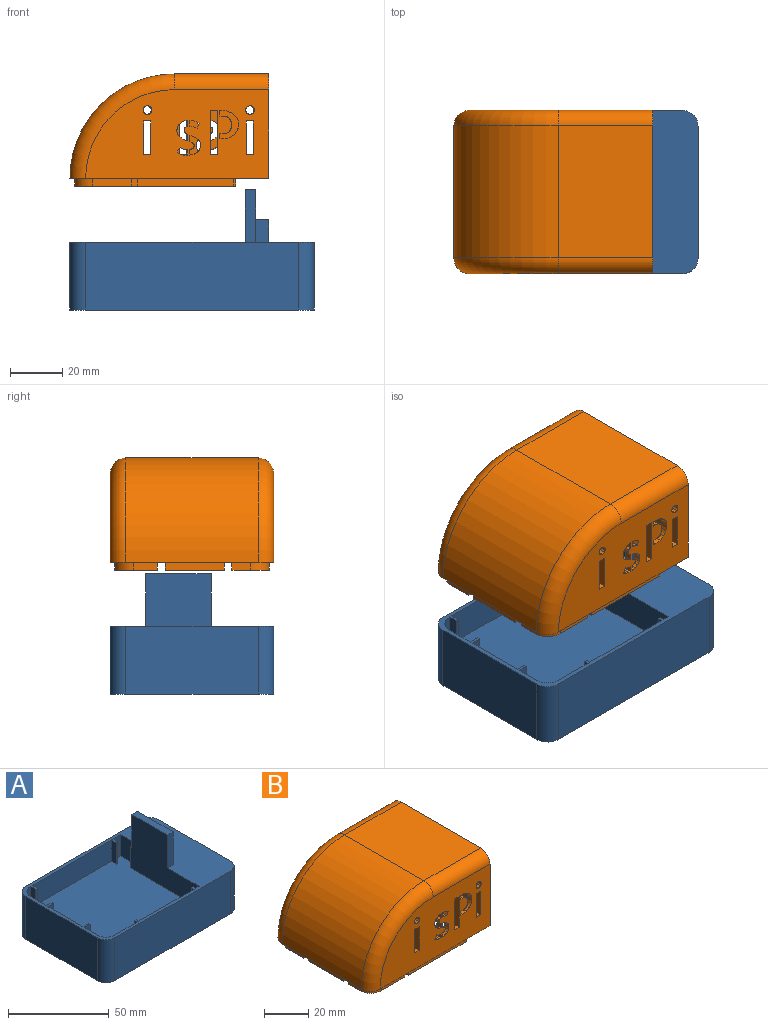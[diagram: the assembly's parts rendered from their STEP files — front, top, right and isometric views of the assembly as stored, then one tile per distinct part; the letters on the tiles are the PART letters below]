
ASSEMBLY  parts=2 mates=1
PART A: 51 faces, bbox 93.5x62.6x46 mm
  f0: plane 93.5x62.6mm, normal (0,0,1), area 1803.2mm2, adj f1,f2,f3,f4,f5,f6,f7,f8
  f1: plane 81.5x26mm, normal (0,-1,0), area 2119mm2, adj f0,f2,f40,f41
  f2: cylinder r=6mm len=26mm, axis (0,0,-1), area 245mm2, adj f0,f1,f3,f41
  f3: plane 50.6x26mm, normal (1,0,0), area 1315.6mm2, adj f0,f2,f4,f41
  f4: cylinder r=6mm len=26mm, axis (0,0,-1), area 245mm2, adj f0,f3,f5,f41
  f5: plane 81.5x26mm, normal (0,1,0), area 2119mm2, adj f0,f4,f6,f41
  f6: cylinder r=6mm len=26mm, axis (0,0,-1), area 245mm2, adj f0,f5,f7,f41
  f7: plane 50.6x26mm, normal (-1,0,0), area 1315.6mm2, adj f0,f6,f40,f41
  f8: plane 24.6x13mm, normal (1,0,0), area 319.8mm2, adj f0,f9,f39,f50
  f9: plane 13x4mm, normal (0,-1,0), area 52mm2, adj f0,f8,f10,f50
  f10: plane 13x1mm, normal (1,0,0), area 13mm2, adj f0,f9,f11,f50
  f11: plane 13x4mm, normal (0,1,0), area 52mm2, adj f0,f10,f12,f50
  f12: plane 13x11.25mm, normal (1,0,0), area 146.2mm2, adj f0,f11,f13,f50
  f13: cylinder r=6mm len=13mm, axis (0,0,-1), area 122.5mm2, adj f0,f12,f14,f50
  f14: plane 13x0.25mm, normal (0,-1,0), area 3.3mm2, adj f0,f13,f15,f50
  f15: plane 13x3.5mm, normal (-1,0,0), area 45.5mm2, adj f0,f14,f16,f50
  f16: plane 13x1mm, normal (0,-1,0), area 13mm2, adj f0,f15,f17,f50
  f17: plane 13x3.5mm, normal (1,0,0), area 45.5mm2, adj f0,f16,f18,f50
  f18: plane 55.6x13mm, normal (0,-1,0), area 722.8mm2, adj f0,f17,f19,f50
  f19: plane 13x3.5mm, normal (-1,0,0), area 45.5mm2, adj f0,f18,f20,f50
  f20: plane 13x1mm, normal (0,-1,0), area 13mm2, adj f0,f19,f21,f50
  f21: plane 13x3.5mm, normal (1,0,0), area 45.5mm2, adj f0,f20,f22,f50
  f22: plane 13x5.6mm, normal (0,-1,0), area 72.8mm2, adj f0,f21,f23,f50
  f23: plane 13x10.6mm, normal (-1,0,0), area 137.8mm2, adj f0,f22,f24,f50
  f24: plane 13x4mm, normal (0,1,0), area 52mm2, adj f0,f23,f25,f50
  f25: plane 48.5x33mm, normal (-1,0,0), area 1130.5mm2, adj f0,f24,f26,f43,f44,f45,f50
  f26: plane 13x2.5mm, normal (0,1,0), area 32.5mm2, adj f0,f25,f27,f50
  f27: plane 13x1.8mm, normal (1,0,0), area 23.4mm2, adj f0,f26,f28,f50
  f28: plane 13x1mm, normal (0,1,0), area 13mm2, adj f0,f27,f29,f50
  f29: plane 13x1.8mm, normal (-1,0,0), area 23.4mm2, adj f0,f28,f30,f50
  f30: plane 39x13mm, normal (0,1,0), area 507mm2, adj f0,f29,f31,f50
  f31: plane 13x1.8mm, normal (1,0,0), area 23.4mm2, adj f0,f30,f32,f50
  f32: plane 13x0.95mm, normal (0,1,0), area 12.3mm2, adj f0,f31,f33,f50
  f33: plane 13x1.8mm, normal (-1,0,0), area 23.4mm2, adj f0,f32,f34,f50
  f34: plane 16x13mm, normal (0,1,0), area 208mm2, adj f0,f33,f35,f50
  f35: cylinder r=6mm len=13mm, axis (0,0,-1), area 122.5mm2, adj f0,f34,f36,f50
  f36: plane 13x9.25mm, normal (1,0,0), area 120.3mm2, adj f0,f35,f37,f50
  f37: plane 13x4mm, normal (0,-1,0), area 52mm2, adj f0,f36,f38,f50
  f38: plane 13x1mm, normal (1,0,0), area 13mm2, adj f0,f37,f39,f50
  f39: plane 13x4mm, normal (0,1,0), area 52mm2, adj f0,f8,f38,f50
  f40: cylinder r=6mm len=26mm, axis (0,0,-1), area 245mm2, adj f0,f1,f7,f41
  f41: plane 93.5x62.6mm, normal (0,0,-1), area 5822.2mm2, adj f1,f2,f3,f4,f5,f6,f7,f40
  f42: plane 25x20mm, normal (1,0,0), area 427.7mm2, adj f0,f43,f44,f45,f46,f47,f49
  f43: plane 20x4mm, normal (0,1,0), area 80mm2, adj f0,f25,f42,f45
  f44: plane 20x4mm, normal (0,-1,0), area 80mm2, adj f0,f25,f42,f45
  f45: plane 25x4mm, normal (0,0,1), area 100mm2, adj f25,f42,f43,f44
  f46: plane 8.5x5mm, normal (0,1,0), area 42.5mm2, adj f0,f42,f48,f49
  f47: plane 8.5x5mm, normal (0,-1,0), area 42.5mm2, adj f0,f42,f48,f49
  f48: plane 8.5x8.5mm, normal (1,0,0), area 72.3mm2, adj f0,f46,f47,f49
  f49: plane 8.5x5mm, normal (0,0,1), area 42.5mm2, adj f42,f46,f47,f48
  f50: plane 69.45x59.1mm, normal (0,0,1), area 3876.5mm2, adj f8,f9,f10,f11,f12,f13,f14,f15
PART B: 242 faces, bbox 79.5x62.6x46.3 mm
  f0: plane 65.45x34.25mm, normal (0,1,0), area 1760mm2, adj f5,f6,f7,f11,f29,f30,f35,f36
  f1: plane 70.2x34mm, normal (0,-1,0), area 1907.2mm2, adj f4,f6,f17,f20,f149,f150,f151,f152
  f2: plane 66.2x35mm, normal (0,-1,0), area 1828mm2, adj f5,f6,f10,f14,f24,f25,f27,f56
  f3: plane 70.2x34mm, normal (0,1,0), area 1907.2mm2, adj f4,f6,f15,f18,f56,f57,f58,f59
  f4: plane 62.6x40mm, normal (1,0,0), area 1909.3mm2, adj f1,f3,f6,f18,f19,f20,f21,f22
  f5: plane 57.1x37.25mm, normal (-1,0,0), area 1532.3mm2, adj f0,f2,f6,f7,f8,f9,f10,f21
  f6: plane 76.2x62.6mm, normal (0,0,-1), area 510mm2, adj f0,f1,f2,f3,f4,f5,f12,f13
  f7: cylinder r=6mm len=34.2mm, axis (-1,0,0), area 322.3mm2, adj f0,f5,f8,f11
  f8: plane 45.1x34.2mm, normal (0,0,-1), area 1542.4mm2, adj f5,f7,f9,f12
  f9: cylinder r=6mm len=34.2mm, axis (-1,0,0), area 296.6mm2, adj f5,f8,f10,f13
  f10: plane 34.2x0.05mm, normal (0,0,-1), area 1.6mm2, adj f2,f5,f9,f14
  f11: torus R=31.25mm, axis (0,-1,0), area 519.2mm2, adj f0,f7,f12,f30
  f12: cylinder r=37.25mm len=45.1mm, axis (0,-1,0), area 2638.9mm2, adj f6,f8,f11,f13,f31,f45,f47
  f13: torus R=31.25mm, axis (0,-1,0), area 481.8mm2, adj f6,f9,f12,f14,f40
  f14: cylinder r=32mm len=32mm, axis (0,-1,0), area 2.4mm2, adj f2,f6,f10,f13
  f15: torus R=34mm, axis (0,-1,0), area 559.9mm2, adj f3,f6,f16,f18
  f16: cylinder r=40mm len=50.6mm, axis (0,-1,0), area 3179.3mm2, adj f6,f15,f17,f19
  f17: torus R=34mm, axis (0,-1,0), area 559.9mm2, adj f1,f6,f16,f20
  f18: cylinder r=6mm len=36.2mm, axis (-1,0,0), area 341.2mm2, adj f3,f4,f15,f19
  f19: plane 50.6x36.2mm, normal (0,0,1), area 1831.7mm2, adj f4,f16,f18,f20
  f20: cylinder r=6mm len=36.2mm, axis (-1,0,0), area 341.2mm2, adj f1,f4,f17,f19
  f21: plane 8.5x2mm, normal (0,1,0), area 17mm2, adj f4,f5,f6,f23
  f22: plane 8.5x2mm, normal (0,-1,0), area 17mm2, adj f4,f5,f6,f23
  f23: plane 8.5x2mm, normal (0,0,-1), area 17mm2, adj f4,f5,f21,f22
  f24: plane 3x1mm, normal (-1,0,0), area 3mm2, adj f2,f6,f26,f27
  f25: plane 3x1mm, normal (1,0,0), area 3mm2, adj f2,f6,f26,f27
  f26: plane 53.6x3mm, normal (0,1,0), area 160.8mm2, adj f6,f24,f25,f27
  f27: plane 53.6x1mm, normal (0,0,-1), area 53.6mm2, adj f2,f24,f25,f26
  f28: plane 14.95x3mm, normal (0,-1,0), area 44.8mm2, adj f6,f29,f34,f35
  f29: plane 3x1mm, normal (1,0,0), area 3mm2, adj f0,f6,f28,f35
  f30: cylinder r=6mm len=6mm, axis (0,0,1), area 28.3mm2, adj f0,f11,f31,f35
  f31: plane 7.25x3mm, normal (1,0,0), area 21.8mm2, adj f12,f30,f32,f35
  f32: plane 3x1mm, normal (0,1,0), area 3mm2, adj f6,f31,f33,f35
  f33: plane 7.25x3mm, normal (-1,0,0), area 21.8mm2, adj f6,f32,f34,f35
  f34: cylinder r=7mm len=7mm, axis (0,0,1), area 33mm2, adj f6,f28,f33,f35
  f35: plane 21.95x14.25mm, normal (0,0,-1), area 32.4mm2, adj f0,f28,f29,f30,f31,f32,f33,f34
  f36: plane 3x1mm, normal (-1,0,0), area 3mm2, adj f0,f6,f37,f39
  f37: plane 36.95x3mm, normal (0,-1,0), area 110.9mm2, adj f6,f36,f38,f39
  f38: plane 3x1mm, normal (1,0,0), area 3mm2, adj f0,f6,f37,f39
  f39: plane 36.95x1mm, normal (0,0,-1), area 36.9mm2, adj f0,f36,f37,f38
  f40: cylinder r=6mm len=5.75mm, axis (0,0,1), area 23.1mm2, adj f13,f41,f45,f46
  f41: plane 3x1.04mm, normal (1,-0.01,0), area 3.1mm2, adj f6,f40,f42,f46
  f42: cylinder r=7mm len=6.79mm, axis (0,0,1), area 27.9mm2, adj f6,f41,f43,f46
  f43: plane 9.25x3mm, normal (-1,0,0), area 27.8mm2, adj f6,f42,f44,f46
  f44: plane 3x1mm, normal (0,-1,0), area 3mm2, adj f6,f43,f45,f46
  f45: plane 9.25x3mm, normal (1,0,0), area 27.8mm2, adj f12,f40,f44,f46
  f46: plane 16.04x5.31mm, normal (0,0,-1), area 17.7mm2, adj f40,f41,f42,f43,f44,f45
  f47: plane 22.6x3mm, normal (1,0,0), area 67.8mm2, adj f12,f48,f50,f51
  f48: plane 3x1mm, normal (0,1,0), area 3mm2, adj f6,f47,f49,f51
  f49: plane 22.6x3mm, normal (-1,0,0), area 67.8mm2, adj f6,f48,f50,f51
  f50: plane 3x1mm, normal (0,-1,0), area 3mm2, adj f6,f47,f49,f51
  f51: plane 22.6x1mm, normal (0,0,-1), area 22.6mm2, adj f47,f48,f49,f50
  f52: cylinder r=4.56mm len=9.13mm, axis (1,0,0), area 41.7mm2, adj f4,f5,f53
  f53: extruded ~20x19.99mm, area 111.6mm2, adj f4,f5,f52
  f54: cylinder r=4.56mm len=9.13mm, axis (1,0,0), area 41.7mm2, adj f4,f5,f55
  f55: extruded ~20x19.99mm, area 111.6mm2, adj f4,f5,f54
  f56: extruded ~2.75x1.09mm, area 3.4mm2, adj f2,f3,f57,f64
  f57: plane 2.75x1.87mm, normal (-0.85,0,-0.53), area 6.1mm2, adj f2,f3,f56,f58
  f58: extruded ~2.75x1.01mm, area 3.2mm2, adj f2,f3,f57,f59
  f59: extruded ~2.75x0.96mm, area 2.8mm2, adj f2,f3,f58,f60
  f60: extruded ~2.75x0.96mm, area 2.7mm2, adj f2,f3,f59,f61
  f61: extruded ~2.75x1.06mm, area 2.9mm2, adj f2,f3,f60,f62
  f62: plane 2.75x2.14mm, normal (1,0,0), area 5.9mm2, adj f2,f3,f61,f63
  f63: plane 2.75x0.11mm, normal (0,0,-1), area 0.3mm2, adj f2,f3,f62,f64
  f64: extruded ~2.75x1.6mm, area 4.5mm2, adj f2,f3,f56,f63
  f65: extruded ~2.75x1.16mm, area 3.6mm2, adj f2,f3,f66,f72
  f66: extruded ~2.75x1.18mm, area 3.6mm2, adj f2,f3,f65,f67
  f67: extruded ~2.75x1.18mm, area 3.6mm2, adj f2,f3,f66,f68
  f68: extruded ~2.75x1.15mm, area 3.5mm2, adj f2,f3,f67,f69
  f69: extruded ~2.75x1.18mm, area 3.6mm2, adj f2,f3,f68,f70
  f70: extruded ~2.75x1.15mm, area 3.5mm2, adj f2,f3,f69,f71
  f71: extruded ~2.75x1.17mm, area 3.6mm2, adj f2,f3,f70,f72
  f72: extruded ~2.75x1.18mm, area 3.6mm2, adj f2,f3,f65,f71
  f73: plane 2.82x2.75mm, normal (0,0,1), area 7.7mm2, adj f2,f3,f74,f76
  f74: plane 13x2.75mm, normal (1,0,0), area 35.8mm2, adj f2,f3,f73,f75
  f75: plane 2.82x2.75mm, normal (0,0,-1), area 7.7mm2, adj f2,f3,f74,f76
  f76: plane 13x2.75mm, normal (-1,0,0), area 35.8mm2, adj f2,f3,f73,f75
  f77: extruded ~2.75x1.33mm, area 3.9mm2, adj f2,f3,f78,f82
  f78: plane 2.75x1.91mm, normal (0.9,0,0.43), area 5.8mm2, adj f2,f3,f77,f79
  f79: extruded ~2.75x1.71mm, area 5.2mm2, adj f2,f3,f78,f80
  f80: extruded ~2.75x1.92mm, area 5.3mm2, adj f2,f3,f79,f81
  f81: plane 2.75x2.28mm, normal (-1,0,0), area 6.3mm2, adj f2,f3,f80,f82
  f82: extruded ~2.75x1.4mm, area 3.9mm2, adj f2,f3,f77,f81
  f83: extruded ~2.75x1.58mm, area 4.5mm2, adj f2,f3,f84,f96
  f84: extruded ~2.75x1.89mm, area 5.6mm2, adj f2,f3,f83,f85
  f85: extruded ~2.75x1.83mm, area 6.3mm2, adj f2,f3,f84,f86
  f86: extruded ~2.75x0.8mm, area 2.4mm2, adj f2,f3,f85,f87
  f87: extruded ~2.75x0.8mm, area 2.3mm2, adj f2,f3,f86,f88
  f88: plane 2.75x2.47mm, normal (1,0,0), area 6.8mm2, adj f2,f3,f87,f89
  f89: extruded ~2.75x0.91mm, area 3mm2, adj f2,f3,f88,f90
  f90: extruded ~2.75x0.89mm, area 2.7mm2, adj f2,f3,f89,f91
  f91: extruded ~2.75x1.04mm, area 3.1mm2, adj f2,f3,f90,f92
  f92: extruded ~2.75x0.93mm, area 2.9mm2, adj f2,f3,f91,f93
  f93: plane 2.75x2.31mm, normal (1,0,0), area 6.3mm2, adj f2,f3,f92,f94
  f94: extruded ~2.75x1.51mm, area 4.3mm2, adj f2,f3,f93,f95
  f95: extruded ~2.75x1.3mm, area 4.2mm2, adj f2,f3,f94,f96
  f96: extruded ~2.75x1.2mm, area 4.2mm2, adj f2,f3,f83,f95
  f97: extruded ~2.75x1.41mm, area 4.1mm2, adj f2,f3,f98,f110
  f98: plane 2.75x2.45mm, normal (-1,0,0), area 6.7mm2, adj f2,f3,f97,f99
  f99: extruded ~2.75x1.17mm, area 3.6mm2, adj f2,f3,f98,f100
  f100: extruded ~2.75x0.93mm, area 3mm2, adj f2,f3,f99,f101
  f101: extruded ~2.75x0.96mm, area 3mm2, adj f2,f3,f100,f102
  f102: extruded ~2.75x1.21mm, area 3.6mm2, adj f2,f3,f101,f103
  f103: plane 2.75x2.19mm, normal (-1,0,0), area 6mm2, adj f2,f3,f102,f104
  f104: extruded ~2.75x1.59mm, area 4.5mm2, adj f2,f3,f103,f105
  f105: extruded ~2.75x1.28mm, area 4.1mm2, adj f2,f3,f104,f106
  f106: extruded ~2.75x1.15mm, area 4mm2, adj f2,f3,f105,f107
  f107: extruded ~2.75x1.57mm, area 4.4mm2, adj f2,f3,f106,f108
  f108: extruded ~2.75x1.53mm, area 4.4mm2, adj f2,f3,f107,f109
  f109: extruded ~2.75x1.03mm, area 3.9mm2, adj f2,f3,f108,f110
  f110: extruded ~2.75x1.3mm, area 4.1mm2, adj f2,f3,f97,f109
  f111: extruded ~2.75x1.16mm, area 3.6mm2, adj f2,f3,f112,f118
  f112: extruded ~2.75x1.18mm, area 3.6mm2, adj f2,f3,f111,f113
  f113: extruded ~2.75x1.18mm, area 3.6mm2, adj f2,f3,f112,f114
  f114: extruded ~2.75x1.15mm, area 3.5mm2, adj f2,f3,f113,f115
  f115: extruded ~2.75x1.18mm, area 3.6mm2, adj f2,f3,f114,f116
  f116: extruded ~2.75x1.15mm, area 3.5mm2, adj f2,f3,f115,f117
  f117: extruded ~2.75x1.17mm, area 3.6mm2, adj f2,f3,f116,f118
  f118: extruded ~2.75x1.18mm, area 3.6mm2, adj f2,f3,f111,f117
  f119: plane 2.77x2.75mm, normal (0,0,-1), area 7.6mm2, adj f2,f3,f120,f122
  f120: plane 16.99x2.75mm, normal (-1,0,0), area 46.7mm2, adj f2,f3,f119,f121
  f121: plane 2.77x2.75mm, normal (0,0,1), area 7.6mm2, adj f2,f3,f120,f122
  f122: plane 16.99x2.75mm, normal (1,0,0), area 46.7mm2, adj f2,f3,f119,f121
  f123: extruded ~2.75x2.15mm, area 6mm2, adj f2,f3,f124,f144
  f124: plane 2.75x1.18mm, normal (0,0,-1), area 3.2mm2, adj f2,f3,f123,f125
  f125: plane 2.75x2.1mm, normal (-1,0,0), area 5.8mm2, adj f2,f3,f124,f126
  f126: plane 2.75x1.13mm, normal (0,0,1), area 3.1mm2, adj f2,f3,f125,f127
  f127: extruded ~2.75x1.71mm, area 4.8mm2, adj f2,f3,f126,f128
  f128: extruded ~2.75x1mm, area 3.6mm2, adj f2,f3,f127,f129
  f129: extruded ~2.75x1.04mm, area 3.2mm2, adj f2,f3,f128,f130
  f130: extruded ~2.75x0.96mm, area 2.7mm2, adj f2,f3,f129,f131
  f131: extruded ~2.75x1.74mm, area 4.9mm2, adj f2,f3,f130,f132
  f132: extruded ~2.75x1.1mm, area 3.6mm2, adj f2,f3,f131,f133
  f133: extruded ~2.75x0.91mm, area 3mm2, adj f2,f3,f132,f134
  f134: extruded ~2.75x1.01mm, area 2.8mm2, adj f2,f3,f133,f135
  f135: plane 2.75x1.59mm, normal (0,0,-1), area 4.4mm2, adj f2,f3,f134,f136
  f136: plane 2.75x2.03mm, normal (-1,0,0), area 5.6mm2, adj f2,f3,f135,f137
  f137: plane 2.75x1.11mm, normal (0,0,1), area 3mm2, adj f2,f3,f136,f138
  f138: extruded ~2.75x2.45mm, area 6.8mm2, adj f2,f3,f137,f139
  f139: extruded ~2.75x1.89mm, area 6.1mm2, adj f2,f3,f138,f140
  f140: extruded ~2.75x1.76mm, area 5.9mm2, adj f2,f3,f139,f141
  f141: extruded ~2.75x2.34mm, area 6.6mm2, adj f2,f3,f140,f142
  f142: extruded ~2.75x2.2mm, area 6.3mm2, adj f2,f3,f141,f143
  f143: extruded ~2.75x1.67mm, area 6mm2, adj f2,f3,f142,f144
  f144: extruded ~2.75x1.9mm, area 6mm2, adj f2,f3,f123,f143
  f145: plane 2.82x2.75mm, normal (0,0,1), area 7.7mm2, adj f2,f3,f146,f148
  f146: plane 13x2.75mm, normal (1,0,0), area 35.8mm2, adj f2,f3,f145,f147
  f147: plane 2.82x2.75mm, normal (0,0,-1), area 7.7mm2, adj f2,f3,f146,f148
  f148: plane 13x2.75mm, normal (-1,0,0), area 35.8mm2, adj f2,f3,f145,f147
  f149: plane 2.82x2.75mm, normal (0,0,1), area 7.7mm2, adj f0,f1,f150,f152
  f150: plane 13x2.75mm, normal (-1,0,0), area 35.8mm2, adj f0,f1,f149,f151
  f151: plane 2.82x2.75mm, normal (0,0,-1), area 7.7mm2, adj f0,f1,f150,f152
  f152: plane 13x2.75mm, normal (1,0,0), area 35.8mm2, adj f0,f1,f149,f151
  f153: plane 2.82x2.75mm, normal (0,0,1), area 7.7mm2, adj f0,f1,f154,f156
  f154: plane 13x2.75mm, normal (-1,0,0), area 35.8mm2, adj f0,f1,f153,f155
  f155: plane 2.82x2.75mm, normal (0,0,-1), area 7.7mm2, adj f0,f1,f154,f156
  f156: plane 13x2.75mm, normal (1,0,0), area 35.8mm2, adj f0,f1,f153,f155
  f157: extruded ~2.75x1.16mm, area 3.6mm2, adj f0,f1,f158,f164
  f158: extruded ~2.75x1.18mm, area 3.6mm2, adj f0,f1,f157,f159
  f159: extruded ~2.75x1.18mm, area 3.6mm2, adj f0,f1,f158,f160
  f160: extruded ~2.75x1.15mm, area 3.5mm2, adj f0,f1,f159,f161
  f161: extruded ~2.75x1.18mm, area 3.6mm2, adj f0,f1,f160,f162
  f162: extruded ~2.75x1.15mm, area 3.5mm2, adj f0,f1,f161,f163
  f163: extruded ~2.75x1.17mm, area 3.6mm2, adj f0,f1,f162,f164
  f164: extruded ~2.75x1.18mm, area 3.6mm2, adj f0,f1,f157,f163
  f165: extruded ~2.75x1.58mm, area 4.5mm2, adj f0,f1,f166,f178
  f166: extruded ~2.75x1.89mm, area 5.6mm2, adj f0,f1,f165,f167
  f167: extruded ~2.75x1.83mm, area 6.3mm2, adj f0,f1,f166,f168
  f168: extruded ~2.75x0.8mm, area 2.4mm2, adj f0,f1,f167,f169
  f169: extruded ~2.75x0.8mm, area 2.3mm2, adj f0,f1,f168,f170
  f170: plane 2.75x2.47mm, normal (-1,0,0), area 6.8mm2, adj f0,f1,f169,f171
  f171: extruded ~2.75x0.91mm, area 3mm2, adj f0,f1,f170,f172
  f172: extruded ~2.75x0.89mm, area 2.7mm2, adj f0,f1,f171,f173
  f173: extruded ~2.75x1.04mm, area 3.1mm2, adj f0,f1,f172,f174
  f174: extruded ~2.75x0.93mm, area 2.9mm2, adj f0,f1,f173,f175
  f175: plane 2.75x2.31mm, normal (-1,0,0), area 6.3mm2, adj f0,f1,f174,f176
  f176: extruded ~2.75x1.51mm, area 4.3mm2, adj f0,f1,f175,f177
  f177: extruded ~2.75x1.3mm, area 4.2mm2, adj f0,f1,f176,f178
  f178: extruded ~2.75x1.2mm, area 4.2mm2, adj f0,f1,f165,f177
  f179: extruded ~2.75x1.33mm, area 3.9mm2, adj f0,f1,f180,f184
  f180: plane 2.75x1.91mm, normal (-0.9,0,0.43), area 5.8mm2, adj f0,f1,f179,f181
  f181: extruded ~2.75x1.71mm, area 5.2mm2, adj f0,f1,f180,f182
  f182: extruded ~2.75x1.92mm, area 5.3mm2, adj f0,f1,f181,f183
  f183: plane 2.75x2.28mm, normal (1,0,0), area 6.3mm2, adj f0,f1,f182,f184
  f184: extruded ~2.75x1.4mm, area 3.9mm2, adj f0,f1,f179,f183
  f185: extruded ~2.75x1.41mm, area 4.1mm2, adj f0,f1,f186,f198
  f186: plane 2.75x2.45mm, normal (1,0,0), area 6.7mm2, adj f0,f1,f185,f187
  f187: extruded ~2.75x1.17mm, area 3.6mm2, adj f0,f1,f186,f188
  f188: extruded ~2.75x0.93mm, area 3mm2, adj f0,f1,f187,f189
  f189: extruded ~2.75x0.96mm, area 3mm2, adj f0,f1,f188,f190
  f190: extruded ~2.75x1.21mm, area 3.6mm2, adj f0,f1,f189,f191
  f191: plane 2.75x2.19mm, normal (1,0,0), area 6mm2, adj f0,f1,f190,f192
  f192: extruded ~2.75x1.59mm, area 4.5mm2, adj f0,f1,f191,f193
  f193: extruded ~2.75x1.28mm, area 4.1mm2, adj f0,f1,f192,f194
  f194: extruded ~2.75x1.15mm, area 4mm2, adj f0,f1,f193,f195
  f195: extruded ~2.75x1.57mm, area 4.4mm2, adj f0,f1,f194,f196
  f196: extruded ~2.75x1.53mm, area 4.4mm2, adj f0,f1,f195,f197
  f197: extruded ~2.75x1.03mm, area 3.9mm2, adj f0,f1,f196,f198
  f198: extruded ~2.75x1.3mm, area 4.1mm2, adj f0,f1,f185,f197
  f199: extruded ~2.75x1.09mm, area 3.4mm2, adj f0,f1,f200,f207
  f200: plane 2.75x1.87mm, normal (0.85,0,-0.53), area 6.1mm2, adj f0,f1,f199,f201
  f201: extruded ~2.75x1.01mm, area 3.2mm2, adj f0,f1,f200,f202
  f202: extruded ~2.75x0.96mm, area 2.8mm2, adj f0,f1,f201,f203
  f203: extruded ~2.75x0.96mm, area 2.7mm2, adj f0,f1,f202,f204
  f204: extruded ~2.75x1.06mm, area 2.9mm2, adj f0,f1,f203,f205
  f205: plane 2.75x2.14mm, normal (-1,0,0), area 5.9mm2, adj f0,f1,f204,f206
  f206: plane 2.75x0.11mm, normal (0,0,-1), area 0.3mm2, adj f0,f1,f205,f207
  f207: extruded ~2.75x1.6mm, area 4.5mm2, adj f0,f1,f199,f206
  f208: plane 2.77x2.75mm, normal (0,0,-1), area 7.6mm2, adj f0,f1,f209,f211
  f209: plane 16.99x2.75mm, normal (1,0,0), area 46.7mm2, adj f0,f1,f208,f210
  f210: plane 2.77x2.75mm, normal (0,0,1), area 7.6mm2, adj f0,f1,f209,f211
  f211: plane 16.99x2.75mm, normal (-1,0,0), area 46.7mm2, adj f0,f1,f208,f210
  f212: extruded ~2.75x2.15mm, area 6mm2, adj f0,f1,f213,f233
  f213: plane 2.75x1.18mm, normal (0,0,-1), area 3.2mm2, adj f0,f1,f212,f214
  f214: plane 2.75x2.1mm, normal (1,0,0), area 5.8mm2, adj f0,f1,f213,f215
  f215: plane 2.75x1.13mm, normal (0,0,1), area 3.1mm2, adj f0,f1,f214,f216
  f216: extruded ~2.75x1.71mm, area 4.8mm2, adj f0,f1,f215,f217
  f217: extruded ~2.75x1mm, area 3.6mm2, adj f0,f1,f216,f218
  f218: extruded ~2.75x1.04mm, area 3.2mm2, adj f0,f1,f217,f219
  f219: extruded ~2.75x0.96mm, area 2.7mm2, adj f0,f1,f218,f220
  f220: extruded ~2.75x1.74mm, area 4.9mm2, adj f0,f1,f219,f221
  f221: extruded ~2.75x1.1mm, area 3.6mm2, adj f0,f1,f220,f222
  f222: extruded ~2.75x0.91mm, area 3mm2, adj f0,f1,f221,f223
  f223: extruded ~2.75x1.01mm, area 2.8mm2, adj f0,f1,f222,f224
  f224: plane 2.75x1.59mm, normal (0,0,-1), area 4.4mm2, adj f0,f1,f223,f225
  f225: plane 2.75x2.03mm, normal (1,0,0), area 5.6mm2, adj f0,f1,f224,f226
  f226: plane 2.75x1.11mm, normal (0,0,1), area 3mm2, adj f0,f1,f225,f227
  f227: extruded ~2.75x2.45mm, area 6.8mm2, adj f0,f1,f226,f228
  f228: extruded ~2.75x1.89mm, area 6.1mm2, adj f0,f1,f227,f229
  f229: extruded ~2.75x1.76mm, area 5.9mm2, adj f0,f1,f228,f230
  f230: extruded ~2.75x2.34mm, area 6.6mm2, adj f0,f1,f229,f231
  f231: extruded ~2.75x2.2mm, area 6.3mm2, adj f0,f1,f230,f232
  f232: extruded ~2.75x1.67mm, area 6mm2, adj f0,f1,f231,f233
  f233: extruded ~2.75x1.9mm, area 6mm2, adj f0,f1,f212,f232
  f234: extruded ~2.75x1.16mm, area 3.6mm2, adj f0,f1,f235,f241
  f235: extruded ~2.75x1.18mm, area 3.6mm2, adj f0,f1,f234,f236
  f236: extruded ~2.75x1.18mm, area 3.6mm2, adj f0,f1,f235,f237
  f237: extruded ~2.75x1.15mm, area 3.5mm2, adj f0,f1,f236,f238
  f238: extruded ~2.75x1.18mm, area 3.6mm2, adj f0,f1,f237,f239
  f239: extruded ~2.75x1.15mm, area 3.5mm2, adj f0,f1,f238,f240
  f240: extruded ~2.75x1.17mm, area 3.6mm2, adj f0,f1,f239,f241
  f241: extruded ~2.75x1.18mm, area 3.6mm2, adj f0,f1,f234,f240
PLACE A t=(-2.33,0.96,-25.3)mm
PLACE B t=(-2.33,0.96,25.11)mm
MATE slider B.f6 <-> A.f40  axis (0,0,-1) through (-43.08,-24.34,25.11)mm
